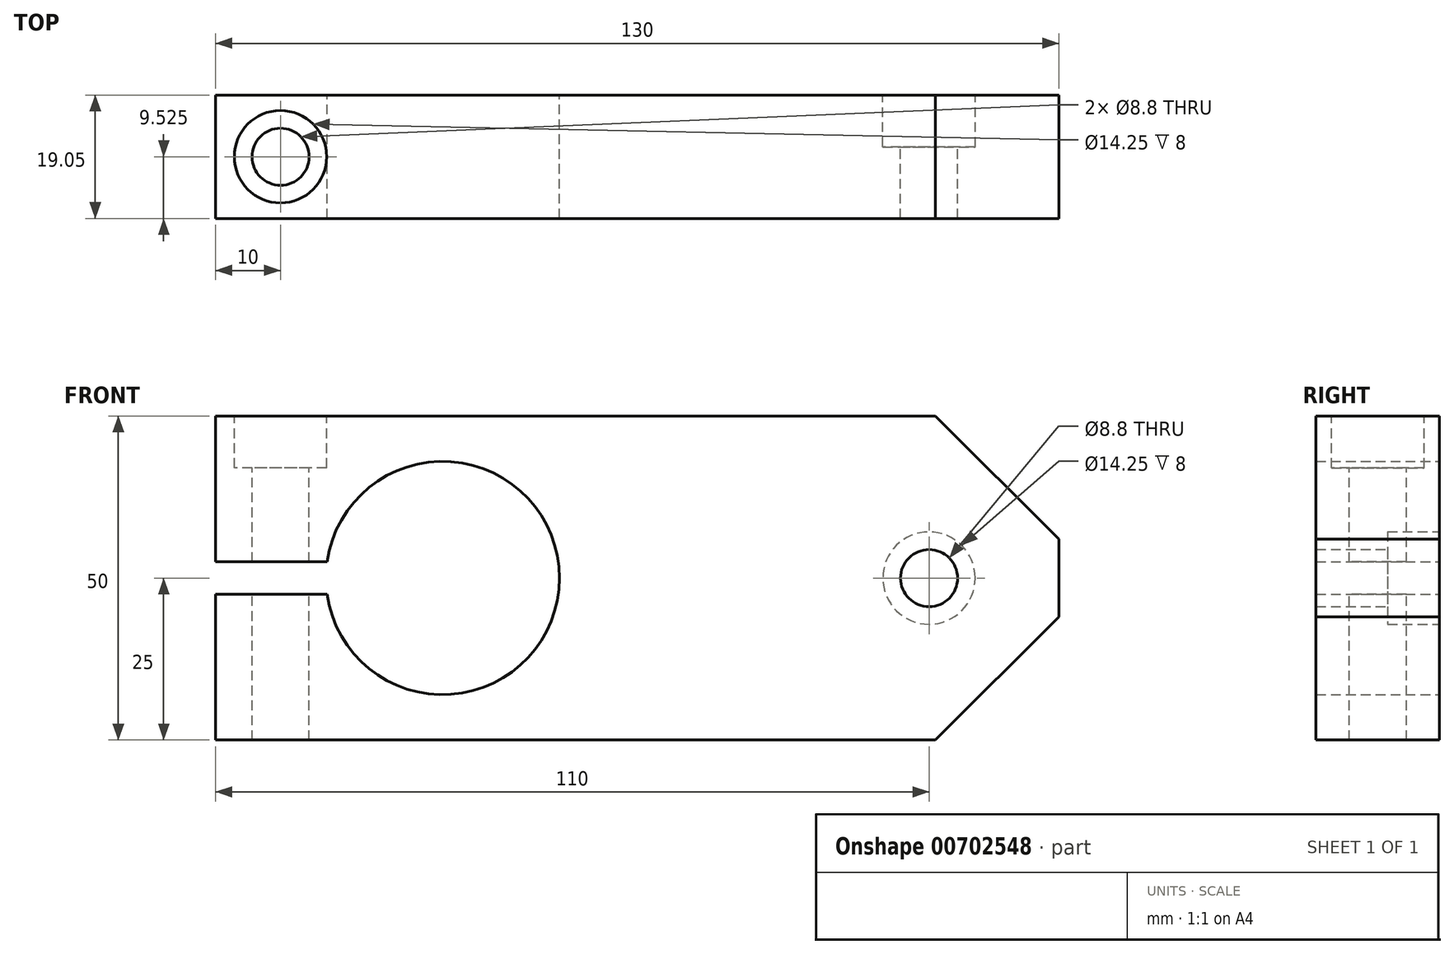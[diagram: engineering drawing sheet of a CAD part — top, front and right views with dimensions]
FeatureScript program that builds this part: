
annotation { "Feature Type Name" : "Feature", "Feature Type Description" : "" }
export const myFeature = defineFeature(function(context is Context, id is Id, definition is map)
    precondition{}
    {
        {
            var Q0;
            Q0=qCreatedBy(makeId("Front.planeOp"),FACE);
            var sketch = newSketch(context, id + "F0", { "sketchPlane" : qUnion([Q0])});
            skLineSegment(sketch, "E0.bottom", {"start": v(0, 0) * mm, "end": v(130, 0) * mm});
            skLineSegment(sketch, "E0.top", {"start": v(0, 50) * mm, "end": v(130, 50) * mm});
            skLineSegment(sketch, "E0.left", {"start": v(0, 0) * mm, "end": v(0, 50) * mm});
            skLineSegment(sketch, "E0.right", {"start": v(130, 0) * mm, "end": v(130, 50) * mm});
            skSolve(sketch);
        }
        {
            var Q0;
            Q0=makeQuery(id+"F0.imprint","IMPRINT",FACE,{"disambiguationData":[TD([[makeQuery(id+"F0.imprint","IMPRINT",EDGE,{"derivedFrom":sQuery(id+"F0.wireOp",EDGE,"E0.bottom")}),1.0]])]});
            extrude(context, id + "F1", {"entities" : qUnion([Q0]), "depth" : 19.05 * mm, "offsetDistance" : 25 * mm});
        }
        {
            var Q0;
            Q0=qCreatedBy(makeId("Front.planeOp"),FACE);
            var sketch = newSketch(context, id + "F2", { "sketchPlane" : qUnion([Q0])});
            skPoint(sketch, "E1", {"position": v(35, 25) * mm});
            skPoint(sketch, "E2", {"position": v(110, 25) * mm});
            skCircle(sketch, "E3", {"center": v(35, 25) * mm, "radius": 18 * mm});
            skSolve(sketch);
        }
        {
            var Q0;
            Q0 = qSketchRegion(id + "F2", true);
            extrude(context, id + "F3", {"entities" : qUnion([Q0]), "operationType" : NewBodyOperationType.REMOVE, "depth" : 40 * mm, "offsetDistance" : 25 * mm});
        }
        {
            var Q0;
            Q0=sQuery(id+"F2.wireOp",VERTEX,"E2");
            var Q1;
            Q1=makeQuery(id+"F1.opExtrude","SWEPT_BODY",BODY,{"disambiguationData":[OSD([sQuery(id+"F0.wireOp",EDGE,"E0.bottom"),sQuery(id+"F0.wireOp",EDGE,"E0.top"),sQuery(id+"F0.wireOp",EDGE,"E0.left"),sQuery(id+"F0.wireOp",EDGE,"E0.right")])]});
            hole(context, id + "F4", {"style" : HoleStyle.C_BORE, "endStyle" : HoleEndStyle.THROUGH, "oppositeDirection" : true, "standardTappedOrClearance" : lookupTablePath({ "standard" : "ISO", "fit" : "Normal", "size" : "M8", "type" : "Clearance" }), "standardBlindInLast" : lookupTablePath({ "fit" : "Standard", "standard" : "ISO", "size" : "M8", "type" : "Clearance" }), "holeDiameter" : 8.8 * mm, "cBoreDiameter" : 14.25 * mm, "cBoreDepth" : 8 * mm, "majorDiameter" : 4 * mm, "isTappedThrough" : true, "tappedDepth" : 17.25 * mm, "tapClearance" : 3, "locations" : qUnion([Q0]), "scope" : qUnion([Q1])});
        }
        {
            var Q0;
            Q0=makeQuery(id+"F1.opExtrude","SWEPT_FACE",FACE,{"disambiguationData":[OSD([sQuery(id+"F0.wireOp",EDGE,"E0.top")])]});
            var sketch = newSketch(context, id + "F5", { "sketchPlane" : qUnion([Q0])});
            skPoint(sketch, "E4", {"position": v(10, -9.53) * mm});
            skPoint(sketch, "E4.positionSnap0", {"position": v(0, -9.53) * mm});
            skSolve(sketch);
        }
        {
            var Q0;
            Q0=sQuery(id+"F5.wireOp",VERTEX,"E4");
            var Q1;
            Q1=makeQuery(id+"F1.opExtrude","SWEPT_BODY",BODY,{"disambiguationData":[OSD([sQuery(id+"F0.wireOp",EDGE,"E0.bottom"),sQuery(id+"F0.wireOp",EDGE,"E0.top"),sQuery(id+"F0.wireOp",EDGE,"E0.left"),sQuery(id+"F0.wireOp",EDGE,"E0.right")])]});
            hole(context, id + "F6", {"style" : HoleStyle.C_BORE, "endStyle" : HoleEndStyle.THROUGH, "standardTappedOrClearance" : lookupTablePath({ "standard" : "ISO", "fit" : "Normal", "size" : "M8", "type" : "Clearance" }), "standardBlindInLast" : lookupTablePath({ "fit" : "Standard", "standard" : "ISO", "size" : "M8", "type" : "Clearance" }), "holeDiameter" : 8.8 * mm, "cBoreDiameter" : 14.25 * mm, "cBoreDepth" : 8 * mm, "majorDiameter" : 5 * mm, "isTappedThrough" : true, "tappedDepth" : 17.25 * mm, "tapClearance" : 3, "locations" : qUnion([Q0]), "scope" : qUnion([Q1])});
        }
        {
            var Q0;
            Q0=makeQuery(id+"F1.opExtrude","CAP_FACE",FACE,{"disambiguationData":[OSD([sQuery(id+"F0.wireOp",EDGE,"E0.bottom"),sQuery(id+"F0.wireOp",EDGE,"E0.top"),sQuery(id+"F0.wireOp",EDGE,"E0.left"),sQuery(id+"F0.wireOp",EDGE,"E0.right")])],"isStart":true});
            var sketch = newSketch(context, id + "F7", { "sketchPlane" : qUnion([Q0])});
            skPoint(sketch, "E5", {"position": v(0, 27.5) * mm});
            skPoint(sketch, "E6", {"position": v(0, 22.5) * mm});
            skLineSegment(sketch, "E7.bottom", {"start": v(0, 27.5) * mm, "end": v(-21.66, 27.5) * mm});
            skLineSegment(sketch, "E7.top", {"start": v(0, 22.5) * mm, "end": v(-21.66, 22.5) * mm});
            skLineSegment(sketch, "E7.left", {"start": v(0, 27.5) * mm, "end": v(0, 22.5) * mm});
            skLineSegment(sketch, "E7.right", {"start": v(-21.66, 27.5) * mm, "end": v(-21.66, 22.5) * mm});
            skSolve(sketch);
        }
        {
            var Q0;
            Q0 = qSketchRegion(id + "F7", true);
            extrude(context, id + "F8", {"entities" : qUnion([Q0]), "operationType" : NewBodyOperationType.REMOVE, "oppositeDirection" : true, "depth" : 40 * mm, "offsetDistance" : 25 * mm});
        }
        {
            var Q0;
            Q0=makeQuery(id+"F1.opExtrude","CAP_FACE",FACE,{"disambiguationData":[OSD([sQuery(id+"F0.wireOp",EDGE,"E0.bottom"),sQuery(id+"F0.wireOp",EDGE,"E0.top"),sQuery(id+"F0.wireOp",EDGE,"E0.left"),sQuery(id+"F0.wireOp",EDGE,"E0.right")])],"isStart":true});
            var sketch = newSketch(context, id + "F9", { "sketchPlane" : qUnion([Q0])});
            skLineSegment(sketch, "E8", {"start": v(-130, 0) * mm, "end": v(-111, 0) * mm});
            skLineSegment(sketch, "E9", {"start": v(-130, 0) * mm, "end": v(-130, 19) * mm});
            skLineSegment(sketch, "E10", {"start": v(-111, 0) * mm, "end": v(-130, 19) * mm});
            skLineSegment(sketch, "E11", {"start": v(-130, 50) * mm, "end": v(-111, 50) * mm});
            skLineSegment(sketch, "E12", {"start": v(-130, 50) * mm, "end": v(-130, 31) * mm});
            skLineSegment(sketch, "E13", {"start": v(-130, 31) * mm, "end": v(-111, 50) * mm});
            skSolve(sketch);
        }
        {
            var Q0;
            Q0=makeQuery(id+"F9.imprint","IMPRINT",FACE,{"disambiguationData":[TD([[makeQuery(id+"F9.imprint","IMPRINT",EDGE,{"derivedFrom":sQuery(id+"F9.wireOp",EDGE,"E8")}),-1.0]])]});
            var Q1;
            Q1=makeQuery(id+"F9.imprint","IMPRINT",FACE,{"disambiguationData":[TD([[makeQuery(id+"F9.imprint","IMPRINT",EDGE,{"derivedFrom":sQuery(id+"F9.wireOp",EDGE,"E11")}),1.0]])]});
            extrude(context, id + "F10", {"entities" : qUnion([Q0, Q1]), "operationType" : NewBodyOperationType.REMOVE, "oppositeDirection" : true, "depth" : 25 * mm, "offsetDistance" : 25 * mm});
        }
    });
